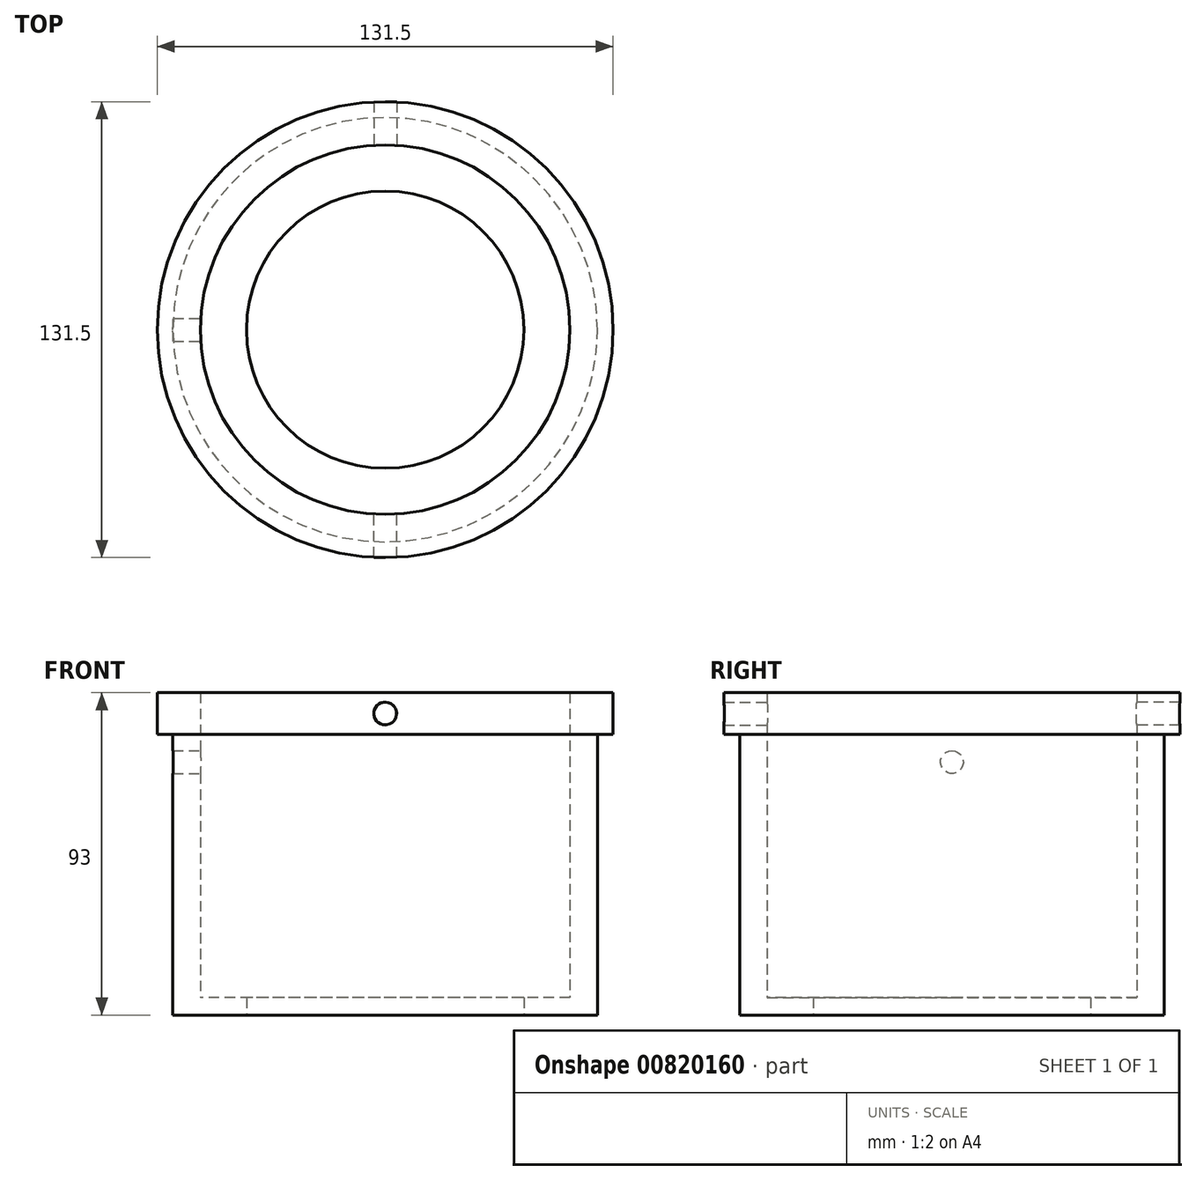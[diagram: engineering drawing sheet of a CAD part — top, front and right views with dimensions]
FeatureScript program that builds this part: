
annotation { "Feature Type Name" : "Feature", "Feature Type Description" : "" }
export const myFeature = defineFeature(function(context is Context, id is Id, definition is map)
    precondition{}
    {
        {
            var Q0;
            Q0=qCreatedBy(makeId("Top.planeOp"),FACE);
            var sketch = newSketch(context, id + "F0", { "sketchPlane" : qUnion([Q0])});
            skCircle(sketch, "E0", {"center": v(0, 0) * mm, "radius": 65.75 * mm});
            skCircle(sketch, "E1", {"center": v(0, 0) * mm, "radius": 53.3 * mm});
            skSolve(sketch);
        }
        {
            var Q0;
            Q0=makeQuery(id+"F0.imprint","IMPRINT",FACE,{"disambiguationData":[TD([[makeQuery(id+"F0.imprint","IMPRINT",EDGE,{"derivedFrom":sQuery(id+"F0.wireOp",EDGE,"E0")}),1.0]])]});
            extrude(context, id + "F1", {"entities" : qUnion([Q0]), "depth" : 93 * mm, "offsetDistance" : 25 * mm});
        }
        {
            var Q0;
            Q0=qCreatedBy(makeId("Top.planeOp"),FACE);
            var sketch = newSketch(context, id + "F2", { "sketchPlane" : qUnion([Q0])});
            skCircle(sketch, "E2", {"center": v(0, 0) * mm, "radius": 40 * mm});
            skCircle(sketch, "E3", {"center": v(0, 0) * mm, "radius": 61.23 * mm});
            skCircle(sketch, "E4", {"center": v(0, 0) * mm, "radius": 75 * mm});
            skSolve(sketch);
        }
        {
            var Q0;
            Q0=makeQuery(id+"F2.imprint","IMPRINT",FACE,{"disambiguationData":[TD([[makeQuery(id+"F2.imprint","IMPRINT",EDGE,{"derivedFrom":sQuery(id+"F2.wireOp",EDGE,"E3")}),-1.0]])]});
            extrude(context, id + "F3", {"entities" : qUnion([Q0]), "operationType" : NewBodyOperationType.REMOVE, "depth" : 81 * mm, "offsetDistance" : 25 * mm});
        }
        {
            var Q0;
            Q0=makeQuery(id+"F2.imprint","IMPRINT",FACE,{"disambiguationData":[TD([[makeQuery(id+"F2.imprint","IMPRINT",EDGE,{"derivedFrom":sQuery(id+"F2.wireOp",EDGE,"E2")}),-1.0]])]});
            extrude(context, id + "F4", {"entities" : qUnion([Q0]), "operationType" : NewBodyOperationType.ADD, "depth" : 5 * mm, "offsetDistance" : 25 * mm});
        }
        {
            var Q0;
            Q0=qCreatedBy(makeId("Front.planeOp"),FACE);
            var sketch = newSketch(context, id + "F5", { "sketchPlane" : qUnion([Q0])});
            skLineSegment(sketch, "E5", {"start": v(0, 0) * mm, "end": v(0, 96.05) * mm, "construction": true});
            skLineSegment(sketch, "E6", {"start": v(0, 87) * mm, "end": v(65.75, 87) * mm, "construction": true});
            skLineSegment(sketch, "E7", {"start": v(65.75, 87) * mm, "end": v(-65.97, 87) * mm, "construction": true});
            skSolve(sketch);
        }
        {
            var Q0;
            Q0=sQuery(id+"F5.wireOp",VERTEX,"E6.start");
            var Q1;
            Q1=makeQuery(id+"F1.opExtrude","SWEPT_BODY",BODY,{"disambiguationData":[OSD([sQuery(id+"F0.wireOp",EDGE,"E0"),sQuery(id+"F0.wireOp",EDGE,"E1")])]});
            hole(context, id + "F6", {"style" : HoleStyle.SIMPLE, "endStyle" : HoleEndStyle.THROUGH, "oppositeDirection" : true, "standardTappedOrClearance" : lookupTablePath({ "standard" : "ISO", "fit" : "Normal", "size" : "M6", "type" : "Clearance" }), "standardBlindInLast" : lookupTablePath({ "fit" : "Standard", "standard" : "ISO", "size" : "M6", "type" : "Clearance" }), "holeDiameter" : 6.6 * mm, "majorDiameter" : 6 * mm, "isTappedThrough" : true, "tappedDepth" : 12 * mm, "tapClearance" : 3, "locations" : qUnion([Q0]), "scope" : qUnion([Q1])});
        }
        {
            var Q0;
            Q0=sQuery(id+"F5.wireOp",VERTEX,"E6.start");
            var Q1;
            Q1=makeQuery(id+"F1.opExtrude","SWEPT_BODY",BODY,{"disambiguationData":[OSD([sQuery(id+"F0.wireOp",EDGE,"E0"),sQuery(id+"F0.wireOp",EDGE,"E1")])]});
            hole(context, id + "F7", {"style" : HoleStyle.SIMPLE, "endStyle" : HoleEndStyle.THROUGH, "standardTappedOrClearance" : lookupTablePath({ "standard" : "ISO", "fit" : "Normal", "size" : "M6", "type" : "Clearance" }), "standardBlindInLast" : lookupTablePath({ "fit" : "Standard", "standard" : "ISO", "size" : "M6", "type" : "Clearance" }), "holeDiameter" : 6.6 * mm, "majorDiameter" : 5 * mm, "isTappedThrough" : true, "tappedDepth" : 12 * mm, "tapClearance" : 3, "locations" : qUnion([Q0]), "scope" : qUnion([Q1])});
        }
        {
            var Q0;
            Q0=qCreatedBy(makeId("Right.planeOp"),FACE);
            var sketch = newSketch(context, id + "F8", { "sketchPlane" : qUnion([Q0])});
            skPoint(sketch, "E8", {"position": v(0, 73) * mm});
            skSolve(sketch);
        }
        {
            var Q0;
            Q0=sQuery(id+"F8.wireOp",VERTEX,"E8");
            var Q1;
            Q1=makeQuery(id+"F1.opExtrude","SWEPT_BODY",BODY,{"disambiguationData":[OSD([sQuery(id+"F0.wireOp",EDGE,"E0"),sQuery(id+"F0.wireOp",EDGE,"E1")])]});
            hole(context, id + "F9", {"style" : HoleStyle.SIMPLE, "endStyle" : HoleEndStyle.BLIND, "standardTappedOrClearance" : lookupTablePath({ "standard" : "ISO", "fit" : "Normal", "size" : "M6", "type" : "Clearance" }), "standardBlindInLast" : lookupTablePath({ "fit" : "Standard", "standard" : "ISO", "size" : "M6", "type" : "Clearance" }), "holeDiameter" : 6.6 * mm, "majorDiameter" : 5 * mm, "holeDepth" : 15 * mm, "isTappedThrough" : true, "tappedDepth" : 12 * mm, "tapClearance" : 3, "locations" : qUnion([Q0]), "scope" : qUnion([Q1])});
        }
    });
